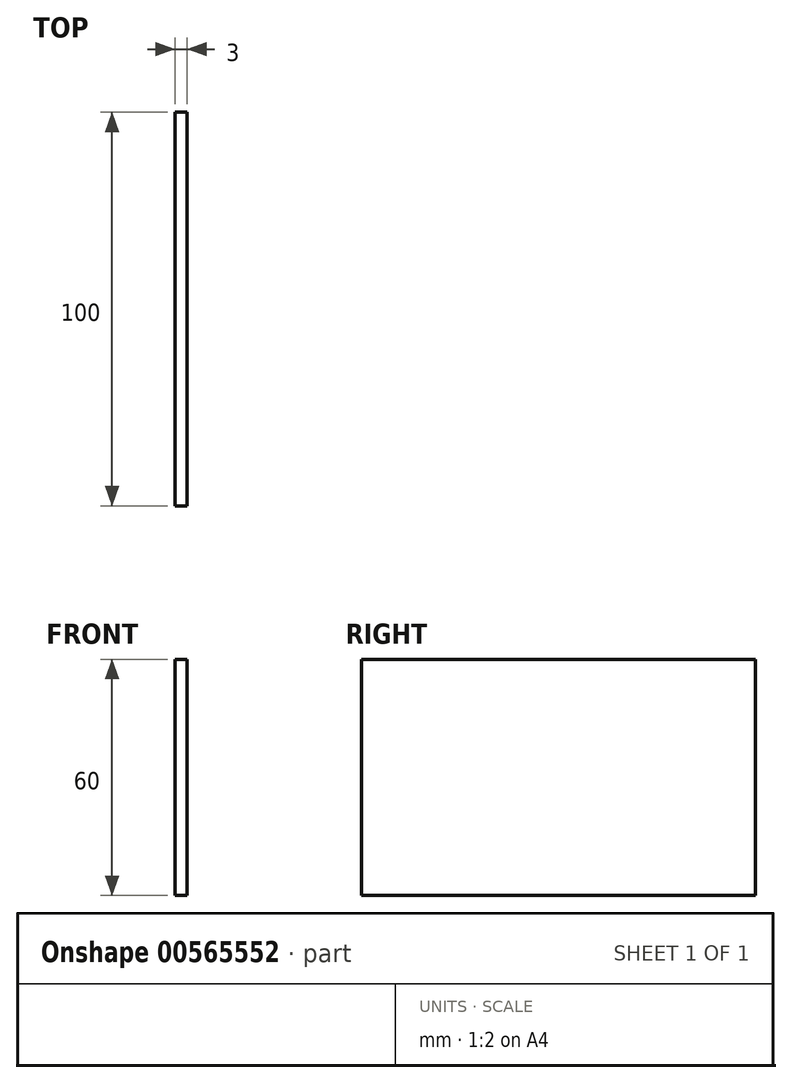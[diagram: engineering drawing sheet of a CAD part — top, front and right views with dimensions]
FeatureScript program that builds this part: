
annotation { "Feature Type Name" : "Feature", "Feature Type Description" : "" }
export const myFeature = defineFeature(function(context is Context, id is Id, definition is map)
    precondition{}
    {
        {
            var Q0;
            Q0=qCreatedBy(makeId("Right.planeOp"),FACE);
            var sketch = newSketch(context, id + "F0", { "sketchPlane" : qUnion([Q0])});
            skLineSegment(sketch, "E0.bottom", {"start": v(50, -30) * mm, "end": v(-50, -30) * mm});
            skLineSegment(sketch, "E0.top", {"start": v(50, 30) * mm, "end": v(-50, 30) * mm});
            skLineSegment(sketch, "E0.left", {"start": v(50, -30) * mm, "end": v(50, 30) * mm});
            skLineSegment(sketch, "E0.right", {"start": v(-50, -30) * mm, "end": v(-50, 30) * mm});
            skPoint(sketch, "E0.middle", {"position": v(0, 0) * mm});
            skSolve(sketch);
        }
        {
            var Q0;
            Q0 = qSketchRegion(id + "F0", true);
            extrude(context, id + "F1", {"entities" : qUnion([Q0]), "depth" : 3 * mm, "offsetDistance" : 25 * mm});
        }
    });
